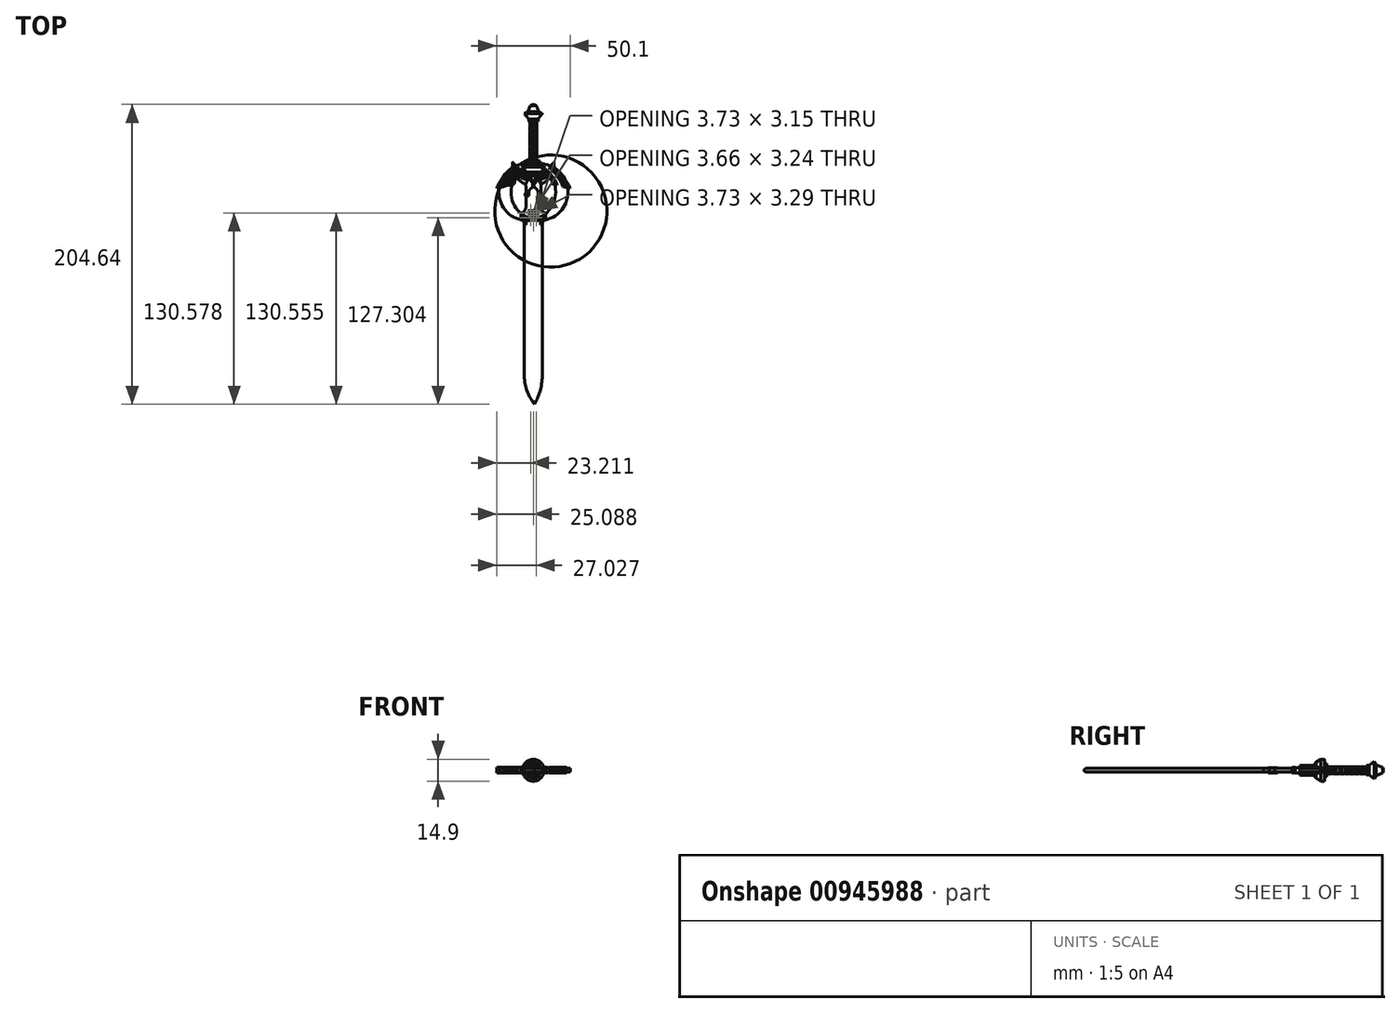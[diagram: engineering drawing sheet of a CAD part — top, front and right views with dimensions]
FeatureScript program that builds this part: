
annotation { "Feature Type Name" : "Feature", "Feature Type Description" : "" }
export const myFeature = defineFeature(function(context is Context, id is Id, definition is map)
    precondition{}
    {
        {
            var Q0;
            Q0=qCreatedBy(makeId("Top.planeOp"),FACE);
            var sketch = newSketch(context, id + "F0", { "sketchPlane" : qUnion([Q0])});
            skLineSegment(sketch, "E0", {"start": v(-5.22, 76.34) * mm, "end": v(-7.23, 75.61) * mm});
            skLineSegment(sketch, "E1", {"start": v(-7.23, 75.61) * mm, "end": v(-8.9, 71.32) * mm});
            skLineSegment(sketch, "E2", {"start": v(-8.9, 71.32) * mm, "end": v(-11.32, 70.05) * mm});
            skLineSegment(sketch, "E3", {"start": v(-11.32, 70.05) * mm, "end": v(-8.36, 66.38) * mm});
            skLineSegment(sketch, "E4", {"start": v(-8.36, 66.38) * mm, "end": v(-8.36, 64.56) * mm});
            skLineSegment(sketch, "E5", {"start": v(-8.36, 64.56) * mm, "end": v(-7.6, 64.56) * mm});
            skLineSegment(sketch, "E6", {"start": v(-7.6, 64.56) * mm, "end": v(-7.6, 37.58) * mm});
            skLineSegment(sketch, "E7", {"start": v(-7.6, 37.58) * mm, "end": v(-9.75, 37.58) * mm});
            skLineSegment(sketch, "E8", {"start": v(-9.75, 37.58) * mm, "end": v(-9.75, 35.78) * mm});
            skLineSegment(sketch, "E9", {"start": v(-9.75, 35.78) * mm, "end": v(-12.69, 35.78) * mm});
            skLineSegment(sketch, "E10", {"start": v(-12.69, 35.78) * mm, "end": v(-12.69, 33.54) * mm});
            skLineSegment(sketch, "E11", {"start": v(-12.69, 33.54) * mm, "end": v(-10.65, 30.07) * mm});
            skLineSegment(sketch, "E12", {"start": v(-10.65, 30.07) * mm, "end": v(-9.23, 28.83) * mm});
            skLineSegment(sketch, "E13", {"start": v(-9.23, 28.83) * mm, "end": v(-6.85, 28.22) * mm});
            skLineSegment(sketch, "E14", {"start": v(-6.85, 28.22) * mm, "end": v(-5.24, 30.4) * mm});
            skLineSegment(sketch, "E15", {"start": v(-5.24, 30.4) * mm, "end": v(-5.22, 76.34) * mm});
            skLineSegment(sketch, "E16", {"start": v(-10.65, 30.07) * mm, "end": v(-10.65, 29.62) * mm});
            skPoint(sketch, "E17.1.internal.snap0", {"position": v(-11.67, 31.8) * mm});
            skFitSpline(sketch, "E17", {"points": [v(-10.65, 29.62) * mm, v(-11.67, 30.16) * mm, v(-14.84, 32.47) * mm, v(-17.18, 34.56) * mm, v(-19.44, 37) * mm], "startDerivative": vector(-5.37, 2.5) * mm, "endDerivative": vector(-8.35, 9.25) * mm});
            skFitSpline(sketch, "E18", {"points": [v(-19.44, 37) * mm, v(-19.44, 35.95) * mm, v(-19.44, 33.83) * mm, v(-19.4, 33.07) * mm, v(-19.44, 33.1) * mm], "startDerivative": vector(0.06, -3.26) * mm, "endDerivative": vector(-1.19, 0.34) * mm});
            skArc(sketch, "E19", {"start": v(-19.4, 33.07) * mm, "mid": v(-25.78, 26.83) * mm, "end": v(-30.3, 19.12) * mm});
            skLineSegment(sketch, "E20", {"start": v(-30.3, 19.12) * mm, "end": v(-18.17, 22.24) * mm});
            skArc(sketch, "E21", {"start": v(-16.35, 26.26) * mm, "mid": v(-17.68, 24.44) * mm, "end": v(-18.17, 22.24) * mm});
            skArc(sketch, "E22", {"start": v(-16.35, 26.26) * mm, "mid": v(-13.8, 23.71) * mm, "end": v(-10.63, 21.98) * mm});
            skArc(sketch, "E23", {"start": v(-16.56, 33.95) * mm, "mid": v(-23.15, 27.52) * mm, "end": v(-28.02, 19.7) * mm});
            skArc(sketch, "E24", {"start": v(-15.75, 33.22) * mm, "mid": v(-21.45, 27.4) * mm, "end": v(-25.51, 20.35) * mm});
            skArc(sketch, "E25", {"start": v(-14.84, 32.47) * mm, "mid": v(-20.11, 27.25) * mm, "end": v(-23.78, 20.8) * mm});
            skArc(sketch, "E26", {"start": v(-14.1, 31.89) * mm, "mid": v(-18.47, 27.05) * mm, "end": v(-21.62, 21.35) * mm});
            skArc(sketch, "E27", {"start": v(-13.5, 31.43) * mm, "mid": v(-17.34, 27.1) * mm, "end": v(-19.75, 21.83) * mm});
            skLineSegment(sketch, "E28", {"start": v(-16.35, 26.26) * mm, "end": v(-12.92, 31) * mm});
            skLineSegment(sketch, "E29", {"start": v(-19.4, 33.07) * mm, "end": v(-17.18, 34.56) * mm});
            skArc(sketch, "E30", {"start": v(-15.35, 27.65) * mm, "mid": v(-12.5, 25.83) * mm, "end": v(-9.23, 24.95) * mm});
            skArc(sketch, "E31", {"start": v(-14.49, 28.83) * mm, "mid": v(-11.25, 27.44) * mm, "end": v(-7.76, 26.93) * mm});
            skArc(sketch, "E32", {"start": v(-13.57, 30.1) * mm, "mid": v(-10.47, 28.76) * mm, "end": v(-7.17, 28) * mm});
            skLineSegment(sketch, "E33", {"start": v(-6.85, 28.22) * mm, "end": v(-10.63, 21.98) * mm});
            skFitSpline(sketch, "E34", {"points": [v(-9.23, 24.95) * mm, v(-8.83, 24.95) * mm], "startDerivative": vector(0.4, 0) * mm, "endDerivative": vector(0.4, 0) * mm});
            skFitSpline(sketch, "E35", {"points": [v(-7.76, 26.93) * mm, v(-7.63, 26.93) * mm], "startDerivative": vector(0.13, 0) * mm, "endDerivative": vector(0.13, 0) * mm});
            skFitSpline(sketch, "E36", {"points": [v(-7.17, 28) * mm, v(-7, 27.99) * mm], "startDerivative": vector(0.17, -0.02) * mm, "endDerivative": vector(0.17, -0.02) * mm});
            skFitSpline(sketch, "E37.MirrorCS", {"points": [v(8.96, 36.98) * mm, v(8.96, 35.93) * mm, v(8.96, 33.81) * mm, v(8.9, 33.06) * mm, v(8.96, 33.08) * mm], "startDerivative": vector(-0.07, -3.26) * mm, "endDerivative": vector(1.19, 0.34) * mm});
            skLineSegment(sketch, "E38.MirrorCS", {"start": v(8.9, 33.06) * mm, "end": v(6.7, 34.54) * mm});
            skLineSegment(sketch, "E39.MirrorCS", {"start": v(5.86, 26.25) * mm, "end": v(2.43, 31) * mm});
            skLineSegment(sketch, "E40.MirrorCS", {"start": v(2.2, 35.77) * mm, "end": v(2.2, 33.53) * mm});
            skPoint(sketch, "E41.MirrorP", {"position": v(1.18, 31.8) * mm});
            skArc(sketch, "E42.MirrorCS", {"start": v(3.62, 31.88) * mm, "mid": v(7.97, 27.04) * mm, "end": v(11.12, 21.33) * mm});
            skArc(sketch, "E43.MirrorCS", {"start": v(5.27, 33.2) * mm, "mid": v(10.96, 27.4) * mm, "end": v(15.01, 20.33) * mm});
            skArc(sketch, "E44.MirrorCS", {"start": v(5.86, 26.25) * mm, "mid": v(7.18, 24.42) * mm, "end": v(7.67, 22.22) * mm});
            skArc(sketch, "E45.MirrorCS", {"start": v(4.36, 32.46) * mm, "mid": v(9.62, 27.23) * mm, "end": v(13.28, 20.78) * mm});
            skArc(sketch, "E46.MirrorCS", {"start": v(3, 31.42) * mm, "mid": v(6.85, 27.09) * mm, "end": v(9.25, 21.82) * mm});
            skLineSegment(sketch, "E47.MirrorCS", {"start": v(0.16, 30.07) * mm, "end": v(0.16, 29.61) * mm});
            skFitSpline(sketch, "E48.MirrorCS", {"points": [v(0.16, 29.61) * mm, v(1.18, 30.15) * mm, v(4.36, 32.46) * mm, v(6.7, 34.54) * mm, v(8.96, 36.98) * mm], "startDerivative": vector(5.37, 2.5) * mm, "endDerivative": vector(8.36, 9.24) * mm});
            skLineSegment(sketch, "E49.MirrorCS", {"start": v(2.2, 33.53) * mm, "end": v(0.16, 30.07) * mm});
            skArc(sketch, "E50.MirrorCS", {"start": v(5.86, 26.25) * mm, "mid": v(3.3, 23.7) * mm, "end": v(0.14, 21.97) * mm});
            skArc(sketch, "E51.MirrorCS", {"start": v(6.07, 33.93) * mm, "mid": v(12.66, 27.5) * mm, "end": v(17.52, 19.68) * mm});
            skArc(sketch, "E52.MirrorCS", {"start": v(8.9, 33.06) * mm, "mid": v(15.29, 26.8) * mm, "end": v(19.8, 19.1) * mm});
            skLineSegment(sketch, "E53.MirrorCS", {"start": v(19.8, 19.1) * mm, "end": v(7.67, 22.22) * mm});
            skFitSpline(sketch, "E54.MirrorCS", {"points": [v(0.16, 29.61) * mm, v(1.18, 30.15) * mm, v(4.36, 32.46) * mm, v(6.7, 34.54) * mm, v(8.96, 36.98) * mm], "startDerivative": vector(5.37, 2.5) * mm, "endDerivative": vector(8.36, 9.24) * mm});
            skArc(sketch, "E55.MirrorCS", {"start": v(4.86, 27.64) * mm, "mid": v(2, 25.82) * mm, "end": v(-1.27, 24.95) * mm});
            skArc(sketch, "E56.MirrorCS", {"start": v(4, 28.82) * mm, "mid": v(0.76, 27.43) * mm, "end": v(-2.73, 26.93) * mm});
            skArc(sketch, "E57.MirrorCS", {"start": v(3.08, 30.1) * mm, "mid": v(-0.02, 28.75) * mm, "end": v(-3.32, 28) * mm});
            skLineSegment(sketch, "E58.MirrorCS", {"start": v(-3.64, 28.22) * mm, "end": v(0.14, 21.97) * mm});
            skLineSegment(sketch, "E59.MirrorCS", {"start": v(0.16, 30.07) * mm, "end": v(-1.26, 28.83) * mm});
            skLineSegment(sketch, "E60.MirrorCS", {"start": v(-1.26, 28.83) * mm, "end": v(-3.64, 28.22) * mm});
            skFitSpline(sketch, "E61.MirrorCS", {"points": [v(-3.32, 28) * mm, v(-3.5, 27.99) * mm], "startDerivative": vector(-0.17, -0.02) * mm, "endDerivative": vector(-0.17, -0.02) * mm});
            skFitSpline(sketch, "E62.MirrorCS", {"points": [v(-2.73, 26.93) * mm, v(-2.86, 26.93) * mm], "startDerivative": vector(-0.13, 0) * mm, "endDerivative": vector(-0.13, 0) * mm});
            skFitSpline(sketch, "E63.MirrorCS", {"points": [v(-1.27, 24.95) * mm, v(-1.66, 24.95) * mm], "startDerivative": vector(-0.4, 0) * mm, "endDerivative": vector(-0.4, 0) * mm});
            skFitSpline(sketch, "E64", {"points": [v(-10.63, 21.98) * mm, v(-10.33, 20.1) * mm, v(-10.37, 18.46) * mm, v(-10.37, 16.67) * mm, v(-10.36, 15.95) * mm], "startDerivative": vector(1.43, -6.77) * mm, "endDerivative": vector(0.02, -3.56) * mm});
            skLineSegment(sketch, "E65", {"start": v(-10.36, 15.95) * mm, "end": v(-8.26, 15.95) * mm});
            skFitSpline(sketch, "E66", {"points": [v(-8.26, 15.95) * mm, v(-8.26, 16.44) * mm, v(-8.13, 17.45) * mm, v(-7.66, 18.2) * mm, v(-6.66, 19.28) * mm, v(-6, 19.75) * mm, v(-5.8, 19.83) * mm], "startDerivative": vector(-0.06, 3.2) * mm, "endDerivative": vector(1.98, 0.65) * mm});
            skFitSpline(sketch, "E67", {"points": [v(-4.62, 19.83) * mm, v(-3.94, 19.37) * mm, v(-3.02, 18.52) * mm, v(-2.42, 17.82) * mm, v(-2.16, 17.16) * mm, v(-2.1, 16.47) * mm, v(-2.1, 15.95) * mm], "startDerivative": vector(3.91, -2.38) * mm, "endDerivative": vector(0.1, -3.68) * mm});
            skLineSegment(sketch, "E68", {"start": v(-2.1, 15.95) * mm, "end": v(-0.16, 15.95) * mm});
            skFitSpline(sketch, "E69.MirrorCS", {"points": [v(0.14, 21.97) * mm, v(-0.17, 20.1) * mm, v(-0.13, 18.46) * mm, v(-0.13, 16.66) * mm, v(-0.14, 15.95) * mm], "startDerivative": vector(-1.44, -6.76) * mm, "endDerivative": vector(-0.02, -3.56) * mm});
            skLineSegment(sketch, "E70", {"start": v(-0.16, 15.95) * mm, "end": v(-0.14, 15.95) * mm});
            skLineSegment(sketch, "E71", {"start": v(-3.64, 28.22) * mm, "end": v(-5.24, 30.4) * mm});
            skLineSegment(sketch, "E72", {"start": v(-8.15, 26.08) * mm, "end": v(-5.86, 22.58) * mm});
            skLineSegment(sketch, "E73", {"start": v(-5.86, 22.58) * mm, "end": v(-5.8, 19.83) * mm});
            skLineSegment(sketch, "E74.MirrorCS", {"start": v(-2.34, 26.08) * mm, "end": v(-4.63, 22.58) * mm});
            skLineSegment(sketch, "E75.MirrorCS", {"start": v(-4.63, 22.58) * mm, "end": v(-4.7, 19.83) * mm});
            skLineSegment(sketch, "E76", {"start": v(-4.7, 19.83) * mm, "end": v(-4.62, 19.83) * mm});
            skLineSegment(sketch, "E77", {"start": v(-10.36, 15.95) * mm, "end": v(-10.95, 15.95) * mm});
            skLineSegment(sketch, "E78", {"start": v(-10.95, 15.95) * mm, "end": v(-10.95, 13.83) * mm});
            skLineSegment(sketch, "E79", {"start": v(-10.95, 13.83) * mm, "end": v(-8.63, 13.83) * mm});
            skLineSegment(sketch, "E80", {"start": v(-8.63, 13.83) * mm, "end": v(-8.27, 13.83) * mm});
            skLineSegment(sketch, "E81", {"start": v(-8.27, 13.83) * mm, "end": v(-8.26, 15.95) * mm});
            skLineSegment(sketch, "E82", {"start": v(-2.1, 15.95) * mm, "end": v(-2.1, 13.83) * mm});
            skLineSegment(sketch, "E83", {"start": v(-2.1, 13.83) * mm, "end": v(0.52, 13.83) * mm});
            skLineSegment(sketch, "E84", {"start": v(0.52, 13.83) * mm, "end": v(0.52, 15.95) * mm});
            skLineSegment(sketch, "E85", {"start": v(0.52, 15.95) * mm, "end": v(-0.16, 15.95) * mm});
            skLineSegment(sketch, "E86", {"start": v(-10.95, 15.26) * mm, "end": v(-8.26, 15.26) * mm});
            skLineSegment(sketch, "E87", {"start": v(-10.95, 14.53) * mm, "end": v(-8.26, 14.53) * mm});
            skLineSegment(sketch, "E88", {"start": v(-2.1, 15.22) * mm, "end": v(0.52, 15.22) * mm});
            skLineSegment(sketch, "E89", {"start": v(-2.1, 14.56) * mm, "end": v(0.52, 14.56) * mm});
            skLineSegment(sketch, "E90", {"start": v(-10.16, 13.83) * mm, "end": v(-10.16, 7.22) * mm});
            skArc(sketch, "E91", {"start": v(-13.54, 1.97) * mm, "mid": v(-11.08, 4.1) * mm, "end": v(-10.16, 7.22) * mm});
            skLineSegment(sketch, "E92", {"start": v(-13.54, 1.97) * mm, "end": v(-13.54, -1.9) * mm});
            skFitSpline(sketch, "E93", {"points": [v(-13.54, -1.9) * mm, v(-12.3, -3.14) * mm, v(-11.8, -3.88) * mm, v(-11.55, -4.81) * mm, v(-11.55, -5.66) * mm], "startDerivative": vector(4.34, -4.17) * mm, "endDerivative": vector(-0.22, -3.77) * mm});
            skLineSegment(sketch, "E94", {"start": v(-11.55, -5.66) * mm, "end": v(-11.55, -107.82) * mm});
            skLineSegment(sketch, "E95.MirrorCS", {"start": v(1.02, -5.67) * mm, "end": v(0.91, -107.82) * mm});
            skLineSegment(sketch, "E96.MirrorCS", {"start": v(-0.34, 13.83) * mm, "end": v(-0.35, 7.21) * mm});
            skArc(sketch, "E97.MirrorCS", {"start": v(3.03, 1.96) * mm, "mid": v(0.56, 4.1) * mm, "end": v(-0.35, 7.21) * mm});
            skLineSegment(sketch, "E98.MirrorCS", {"start": v(3.03, 1.96) * mm, "end": v(3.02, -1.91) * mm});
            skFitSpline(sketch, "E99.MirrorCS", {"points": [v(3.02, -1.91) * mm, v(1.78, -3.15) * mm, v(1.28, -3.9) * mm, v(1.02, -4.82) * mm, v(1.02, -5.67) * mm], "startDerivative": vector(-4.35, -4.17) * mm, "endDerivative": vector(0.22, -3.77) * mm});
            skArc(sketch, "E100", {"start": v(-11.55, -107.82) * mm, "mid": v(-9.73, -118.65) * mm, "end": v(-4.5, -128.3) * mm});
            skArc(sketch, "E101", {"start": v(-4.5, -128.3) * mm, "mid": v(-0.47, -118.4) * mm, "end": v(0.91, -107.82) * mm});
            skLineSegment(sketch, "E102", {"start": v(-4.7, 19.83) * mm, "end": v(-5.24, 19.13) * mm});
            skLineSegment(sketch, "E103", {"start": v(-5.24, 19.13) * mm, "end": v(-5.8, 19.83) * mm});
            skLineSegment(sketch, "E104", {"start": v(-0.34, 13.83) * mm, "end": v(-0.34, 13.83) * mm});
            skSolve(sketch);
        }
        {
            var Q0;
            Q0=makeQuery(id+"F0.imprint","IMPRINT",FACE,{"disambiguationData":[TD([[makeQuery(id+"F0.imprint","IMPRINT",EDGE,{"derivedFrom":sQuery(id+"F0.wireOp",EDGE,"E0")}),1.0]])]});
            var Q1;
            Q1=sQuery(id+"F0.wireOp",EDGE,"E15");
            revolve(context, id + "F1", {"surfaceOperationType" : NewSurfaceOperationType.NEW, "entities" : qUnion([Q0]), "axis" : qUnion([Q1]), "revolveType" : RevolveType.FULL});
        }
        {
            var Q0;
            {var subQ1=sQuery(id+"F0.wireOp",EDGE,"E22");Q0=makeQuery(id+"F0.imprint","IMPRINT",FACE,{"disambiguationData":[TD([[makeQuery(id+"F0.imprint","IMPRINT",EDGE,{"derivedFrom":subQ1}),1.0]])]});}
            var Q1;
            {var subQ2=sQuery(id+"F0.wireOp",EDGE,"E19");Q1=makeQuery(id+"F0.imprint","IMPRINT",FACE,{"disambiguationData":[TD([[makeQuery(id+"F0.imprint","IMPRINT",EDGE,{"derivedFrom":subQ2}),1.0]])]});}
            var Q2;
            {var subQ3=sQuery(id+"F0.wireOp",EDGE,"E55.MirrorCS");Q2=makeQuery(id+"F0.imprint","IMPRINT",FACE,{"disambiguationData":[TD([[makeQuery(id+"F0.imprint","IMPRINT",EDGE,{"derivedFrom":subQ3}),1.0]])]});}
            var Q3;
            {var subQ5=sQuery(id+"F0.wireOp",EDGE,"E51.MirrorCS");Q3=makeQuery(id+"F0.imprint","IMPRINT",FACE,{"disambiguationData":[TD([[makeQuery(id+"F0.imprint","IMPRINT",EDGE,{"derivedFrom":subQ5}),1.0]])]});}
            extrude(context, id + "F2", {"entities" : qUnion([Q0, Q1, Q2, Q3]), "endBound" : BoundingType.SYMMETRIC, "depth" : 3.86 * mm, "offsetDistance" : 25.4 * mm});
        }
        {
            var Q0;
            {var subQ0=sQuery(id+"F0.wireOp",EDGE,"E23");Q0=makeQuery(id+"F0.imprint","IMPRINT",FACE,{"disambiguationData":[TD([[makeQuery(id+"F0.imprint","IMPRINT",EDGE,{"derivedFrom":subQ0}),1.0]])]});}
            var Q1;
            {var subQ4=sQuery(id+"F0.wireOp",EDGE,"E30");Q1=makeQuery(id+"F0.imprint","IMPRINT",FACE,{"disambiguationData":[TD([[makeQuery(id+"F0.imprint","IMPRINT",EDGE,{"derivedFrom":subQ4}),1.0]])]});}
            var Q2;
            {var subQ3=sQuery(id+"F0.wireOp",EDGE,"E55.MirrorCS");Q2=makeQuery(id+"F0.imprint","IMPRINT",FACE,{"disambiguationData":[TD([[makeQuery(id+"F0.imprint","IMPRINT",EDGE,{"derivedFrom":subQ3}),-1.0]])]});}
            var Q3;
            {var subQ0=sQuery(id+"F0.wireOp",EDGE,"E51.MirrorCS");Q3=makeQuery(id+"F0.imprint","IMPRINT",FACE,{"disambiguationData":[TD([[makeQuery(id+"F0.imprint","IMPRINT",EDGE,{"derivedFrom":subQ0}),-1.0]])]});}
            extrude(context, id + "F3", {"entities" : qUnion([Q0, Q1, Q2, Q3]), "endBound" : BoundingType.SYMMETRIC, "depth" : 2.54 * mm, "offsetDistance" : 25.4 * mm});
        }
        {
            var Q0;
            {var subQ0=sQuery(id+"F0.wireOp",EDGE,"E24");Q0=makeQuery(id+"F0.imprint","IMPRINT",FACE,{"disambiguationData":[TD([[makeQuery(id+"F0.imprint","IMPRINT",EDGE,{"derivedFrom":subQ0}),1.0]])]});}
            var Q1;
            {var subQ4=sQuery(id+"F0.wireOp",EDGE,"E31");Q1=makeQuery(id+"F0.imprint","IMPRINT",FACE,{"disambiguationData":[TD([[makeQuery(id+"F0.imprint","IMPRINT",EDGE,{"derivedFrom":subQ4}),1.0]])]});}
            var Q2;
            {var subQ0=sQuery(id+"F0.wireOp",EDGE,"E43.MirrorCS");Q2=makeQuery(id+"F0.imprint","IMPRINT",FACE,{"disambiguationData":[TD([[makeQuery(id+"F0.imprint","IMPRINT",EDGE,{"derivedFrom":subQ0}),-1.0]])]});}
            var Q3;
            {var subQ3=sQuery(id+"F0.wireOp",EDGE,"E56.MirrorCS");Q3=makeQuery(id+"F0.imprint","IMPRINT",FACE,{"disambiguationData":[TD([[makeQuery(id+"F0.imprint","IMPRINT",EDGE,{"derivedFrom":subQ3}),-1.0]])]});}
            extrude(context, id + "F4", {"entities" : qUnion([Q0, Q1, Q2, Q3]), "endBound" : BoundingType.SYMMETRIC, "depth" : 1.93 * mm, "offsetDistance" : 25.4 * mm});
        }
        {
            var Q0;
            Q0=makeQuery(id+"F0.imprint","IMPRINT",FACE,{"disambiguationData":[TD([[makeQuery(id+"F0.imprint","IMPRINT",EDGE,{"derivedFrom":sQuery(id+"F0.wireOp",EDGE,"E12")}),-1.0]])]});
            var Q1;
            {var subQ0=sQuery(id+"F0.wireOp",EDGE,"E25");Q1=makeQuery(id+"F0.imprint","IMPRINT",FACE,{"disambiguationData":[TD([[makeQuery(id+"F0.imprint","IMPRINT",EDGE,{"derivedFrom":subQ0}),1.0]])]});}
            var Q2;
            {var subQ2=sQuery(id+"F0.wireOp",EDGE,"E47.MirrorCS");Q2=makeQuery(id+"F0.imprint","IMPRINT",FACE,{"disambiguationData":[TD([[makeQuery(id+"F0.imprint","IMPRINT",EDGE,{"derivedFrom":subQ2}),-1.0]])]});}
            var Q3;
            {var subQ0=sQuery(id+"F0.wireOp",EDGE,"E42.MirrorCS");Q3=makeQuery(id+"F0.imprint","IMPRINT",FACE,{"disambiguationData":[TD([[makeQuery(id+"F0.imprint","IMPRINT",EDGE,{"derivedFrom":subQ0}),1.0]])]});}
            extrude(context, id + "F5", {"entities" : qUnion([Q0, Q1, Q2, Q3]), "endBound" : BoundingType.SYMMETRIC, "depth" : 1.47 * mm, "offsetDistance" : 25.4 * mm});
        }
        {
            var Q0;
            {var subQ0=sQuery(id+"F0.wireOp",EDGE,"E46.MirrorCS");Q0=makeQuery(id+"F0.imprint","IMPRINT",FACE,{"disambiguationData":[TD([[makeQuery(id+"F0.imprint","IMPRINT",EDGE,{"derivedFrom":subQ0}),1.0]])]});}
            var Q1;
            {var subQ0=sQuery(id+"F0.wireOp",EDGE,"E26");Q1=makeQuery(id+"F0.imprint","IMPRINT",FACE,{"disambiguationData":[TD([[makeQuery(id+"F0.imprint","IMPRINT",EDGE,{"derivedFrom":subQ0}),1.0]])]});}
            extrude(context, id + "F6", {"entities" : qUnion([Q0, Q1]), "endBound" : BoundingType.SYMMETRIC, "oppositeDirection" : true, "depth" : 1.02 * mm, "offsetDistance" : 25.4 * mm});
        }
        {
            var Q0;
            {var subQ6=sQuery(id+"F0.wireOp",EDGE,"E44.MirrorCS");Q0=makeQuery(id+"F0.imprint","IMPRINT",FACE,{"disambiguationData":[TD([[makeQuery(id+"F0.imprint","IMPRINT",EDGE,{"derivedFrom":subQ6}),1.0]])]});}
            var Q1;
            {var subQ1=sQuery(id+"F0.wireOp",EDGE,"E21");Q1=makeQuery(id+"F0.imprint","IMPRINT",FACE,{"disambiguationData":[TD([[makeQuery(id+"F0.imprint","IMPRINT",EDGE,{"derivedFrom":subQ1}),-1.0]])]});}
            extrude(context, id + "F7", {"entities" : qUnion([Q0, Q1]), "endBound" : BoundingType.SYMMETRIC, "depth" : 0.76 * mm, "offsetDistance" : 25.4 * mm});
        }
        {
            var Q0;
            {var subQ6=sQuery(id+"F0.wireOp",EDGE,"E14");Q0=makeQuery(id+"F0.imprint","IMPRINT",FACE,{"disambiguationData":[TD([[makeQuery(id+"F0.imprint","IMPRINT",EDGE,{"derivedFrom":subQ6}),-1.0]])]});}
            extrude(context, id + "F8", {"entities" : qUnion([Q0]), "endBound" : BoundingType.SYMMETRIC, "depth" : 6.6 * mm, "offsetDistance" : 25.4 * mm});
        }
        {
            var Q0;
            Q0=makeQuery(id+"F0.imprint","IMPRINT",FACE,{"disambiguationData":[TD([[makeQuery(id+"F0.imprint","IMPRINT",EDGE,{"derivedFrom":sQuery(id+"F0.wireOp",EDGE,"E67")}),1.0]])]});
            var Q1;
            {var subQ0=sQuery(id+"F0.wireOp",EDGE,"E64");Q1=makeQuery(id+"F0.imprint","IMPRINT",FACE,{"disambiguationData":[TD([[makeQuery(id+"F0.imprint","IMPRINT",EDGE,{"derivedFrom":subQ0}),1.0]])]});}
            extrude(context, id + "F9", {"entities" : qUnion([Q0, Q1]), "endBound" : BoundingType.SYMMETRIC, "depth" : 3.56 * mm, "offsetDistance" : 25.4 * mm});
        }
        {
            var Q0;
            Q0=makeQuery(id+"F8.opExtrude","CAP_EDGE",EDGE,{"disambiguationData":[OSD([sQuery(id+"F0.wireOp",EDGE,"E33")])],"isStart":false});
            var Q1;
            Q1=makeQuery(id+"F8.opExtrude","CAP_EDGE",EDGE,{"disambiguationData":[OSD([sQuery(id+"F0.wireOp",EDGE,"E58.MirrorCS")])],"isStart":false});
            var Q2;
            Q2=makeQuery(id+"F8.opExtrude","CAP_EDGE",EDGE,{"disambiguationData":[OSD([sQuery(id+"F0.wireOp",EDGE,"E72")])],"isStart":false});
            var Q3;
            Q3=makeQuery(id+"F8.opExtrude","CAP_EDGE",EDGE,{"disambiguationData":[OSD([sQuery(id+"F0.wireOp",EDGE,"E74.MirrorCS")])],"isStart":false});
            var Q4;
            Q4=makeQuery(id+"F8.opExtrude","CAP_EDGE",EDGE,{"disambiguationData":[OSD([sQuery(id+"F0.wireOp",EDGE,"E72")])],"isStart":true});
            var Q5;
            Q5=makeQuery(id+"F8.opExtrude","CAP_EDGE",EDGE,{"disambiguationData":[OSD([sQuery(id+"F0.wireOp",EDGE,"E33")])],"isStart":true});
            var Q6;
            Q6=makeQuery(id+"F8.opExtrude","CAP_EDGE",EDGE,{"disambiguationData":[OSD([sQuery(id+"F0.wireOp",EDGE,"E58.MirrorCS")])],"isStart":true});
            var Q7;
            Q7=makeQuery(id+"F8.opExtrude","CAP_EDGE",EDGE,{"disambiguationData":[OSD([sQuery(id+"F0.wireOp",EDGE,"E74.MirrorCS")])],"isStart":true});
            chamfer(context, id + "F10", {"entities" : qUnion([Q0, Q1, Q2, Q3, Q4, Q5, Q6, Q7]), "width" : 1.02 * mm, "tangentPropagation" : true});
        }
        {
            var Q0;
            Q0=makeQuery(id+"F8.opExtrude","CAP_EDGE",EDGE,{"disambiguationData":[OSD([sQuery(id+"F0.wireOp",EDGE,"E73")])],"isStart":false});
            var Q1;
            Q1=makeQuery(id+"F8.opExtrude","CAP_EDGE",EDGE,{"disambiguationData":[OSD([sQuery(id+"F0.wireOp",EDGE,"E75.MirrorCS")])],"isStart":false});
            var Q2;
            Q2=makeQuery(id+"F8.opExtrude","CAP_EDGE",EDGE,{"disambiguationData":[OSD([sQuery(id+"F0.wireOp",EDGE,"E73")])],"isStart":true});
            var Q3;
            Q3=makeQuery(id+"F8.opExtrude","CAP_EDGE",EDGE,{"disambiguationData":[OSD([sQuery(id+"F0.wireOp",EDGE,"E75.MirrorCS")])],"isStart":true});
            chamfer(context, id + "F11", {"entities" : qUnion([Q0, Q1, Q2, Q3]), "width" : 0.5 * mm, "tangentPropagation" : true});
        }
        {
            var Q0;
            {var subQ1=sQuery(id+"F0.wireOp",EDGE,"E65");Q0=makeQuery(id+"F0.imprint","IMPRINT",FACE,{"disambiguationData":[TD([[makeQuery(id+"F0.imprint","IMPRINT",EDGE,{"derivedFrom":subQ1}),-1.0]])]});}
            var Q1;
            {var subQ5=sQuery(id+"F0.wireOp",EDGE,"E68");Q1=makeQuery(id+"F0.imprint","IMPRINT",FACE,{"disambiguationData":[TD([[makeQuery(id+"F0.imprint","IMPRINT",EDGE,{"derivedFrom":subQ5}),-1.0]])]});}
            var Q2;
            {var subQ0=sQuery(id+"F0.wireOp",EDGE,"E80");Q2=makeQuery(id+"F0.imprint","IMPRINT",FACE,{"disambiguationData":[TD([[makeQuery(id+"F0.imprint","IMPRINT",EDGE,{"derivedFrom":subQ0}),1.0]])]});}
            var Q3;
            {var subQ0=sQuery(id+"F0.wireOp",EDGE,"E83");Q3=makeQuery(id+"F0.imprint","IMPRINT",FACE,{"disambiguationData":[TD([[makeQuery(id+"F0.imprint","IMPRINT",EDGE,{"derivedFrom":subQ0}),1.0]])]});}
            extrude(context, id + "F12", {"entities" : qUnion([Q0, Q1, Q2, Q3]), "endBound" : BoundingType.SYMMETRIC, "depth" : 3.91 * mm, "offsetDistance" : 25.4 * mm});
        }
        {
            var Q0;
            {var subQ0=sQuery(id+"F0.wireOp",EDGE,"E86");Q0=makeQuery(id+"F0.imprint","IMPRINT",FACE,{"disambiguationData":[TD([[makeQuery(id+"F0.imprint","IMPRINT",EDGE,{"derivedFrom":subQ0}),-1.0]])]});}
            var Q1;
            {var subQ0=sQuery(id+"F0.wireOp",EDGE,"E88");Q1=makeQuery(id+"F0.imprint","IMPRINT",FACE,{"disambiguationData":[TD([[makeQuery(id+"F0.imprint","IMPRINT",EDGE,{"derivedFrom":subQ0}),-1.0]])]});}
            extrude(context, id + "F13", {"entities" : qUnion([Q0, Q1]), "endBound" : BoundingType.SYMMETRIC, "depth" : 3.15 * mm, "offsetDistance" : 25.4 * mm});
        }
        {
            var Q0;
            {var subQ10=sQuery(id+"F0.wireOp",EDGE,"E66");Q0=makeQuery(id+"F0.imprint","IMPRINT",FACE,{"disambiguationData":[TD([[makeQuery(id+"F0.imprint","IMPRINT",EDGE,{"derivedFrom":subQ10}),-1.0]])]});}
            extrude(context, id + "F14", {"entities" : qUnion([Q0]), "endBound" : BoundingType.SYMMETRIC, "depth" : 2.54 * mm, "offsetDistance" : 25.4 * mm});
        }
        {
            var Q0;
            Q0=makeQuery(id+"F14.opExtrude","CAP_EDGE",EDGE,{"disambiguationData":[OSD([sQuery(id+"F0.wireOp",EDGE,"E96.MirrorCS")])],"isStart":false});
            var Q1;
            Q1=makeQuery(id+"F14.opExtrude","CAP_EDGE",EDGE,{"disambiguationData":[OSD([sQuery(id+"F0.wireOp",EDGE,"E90")])],"isStart":false});
            var Q2;
            Q2=makeQuery(id+"F14.opExtrude","CAP_EDGE",EDGE,{"disambiguationData":[OSD([sQuery(id+"F0.wireOp",EDGE,"E95.MirrorCS")])],"isStart":false});
            var Q3;
            Q3=makeQuery(id+"F14.opExtrude","CAP_EDGE",EDGE,{"disambiguationData":[OSD([sQuery(id+"F0.wireOp",EDGE,"E94")])],"isStart":false});
            fillet(context, id + "F15", {"entities" : qUnion([Q0, Q1, Q2, Q3]), "radius" : 1.27 * mm, "tangentPropagation" : true, "allowEdgeOverflow" : false});
        }
        {
            var Q0;
            Q0=makeQuery(id+"F14.opExtrude","CAP_EDGE",EDGE,{"disambiguationData":[OSD([sQuery(id+"F0.wireOp",EDGE,"E101")])],"isStart":true});
            var Q1;
            Q1=makeQuery(id+"F14.opExtrude","CAP_EDGE",EDGE,{"disambiguationData":[OSD([sQuery(id+"F0.wireOp",EDGE,"E100")])],"isStart":true});
            var Q2;
            Q2=makeQuery(id+"F14.opExtrude","CAP_EDGE",EDGE,{"disambiguationData":[OSD([sQuery(id+"F0.wireOp",EDGE,"E95.MirrorCS")])],"isStart":true});
            var Q3;
            Q3=makeQuery(id+"F14.opExtrude","CAP_EDGE",EDGE,{"disambiguationData":[OSD([sQuery(id+"F0.wireOp",EDGE,"E94")])],"isStart":true});
            var Q4;
            Q4=makeQuery(id+"F14.opExtrude","CAP_EDGE",EDGE,{"disambiguationData":[OSD([sQuery(id+"F0.wireOp",EDGE,"E91")])],"isStart":true});
            var Q5;
            Q5=makeQuery(id+"F14.opExtrude","CAP_EDGE",EDGE,{"disambiguationData":[OSD([sQuery(id+"F0.wireOp",EDGE,"E97.MirrorCS")])],"isStart":true});
            fillet(context, id + "F16", {"entities" : qUnion([Q0, Q1, Q2, Q3, Q4, Q5]), "radius" : 1.27 * mm, "tangentPropagation" : true, "allowEdgeOverflow" : false});
        }
        {
            var Q0;
            {var subQ0=sQuery(id+"F0.wireOp",EDGE,"E18");var subQ1=sQuery(id+"F0.wireOp",EDGE,"E17");var subQ2=makeQuery(id+"F0.imprint","INTERSECT",VERTEX,{"derivedFrom":[subQ1,subQ0]});Q0=makeQuery(id+"F0.imprint","IMPRINT",FACE,{"disambiguationData":[TD([[makeQuery(id+"F0.imprint","IMPRINT",EDGE,{"disambiguationData":[TD([[subQ2,1.0]])],"derivedFrom":subQ1}),1.0]])]});}
            var Q1;
            {var subQ0=sQuery(id+"F0.wireOp",EDGE,"E54.MirrorCS");var subQ1=sQuery(id+"F0.wireOp",EDGE,"E37.MirrorCS");var subQ2=makeQuery(id+"F0.imprint","INTERSECT",VERTEX,{"derivedFrom":[subQ1,subQ0]});Q1=makeQuery(id+"F0.imprint","IMPRINT",FACE,{"disambiguationData":[TD([[makeQuery(id+"F0.imprint","IMPRINT",EDGE,{"disambiguationData":[TD([[subQ2,-1.0]])],"derivedFrom":subQ1}),-1.0]])]});}
            extrude(context, id + "F17", {"entities" : qUnion([Q0, Q1]), "endBound" : BoundingType.SYMMETRIC, "depth" : 1.93 * mm, "offsetDistance" : 25.4 * mm});
        }
        {
            var Q0;
            Q0=qCreatedBy(makeId("Top.planeOp"),FACE);
            cPlane(context, id + "F18", {"entities" : qUnion([Q0]), "cplaneType" : CPlaneType.OFFSET, "offset" : 24.13 * mm, "width" : 152.4 * mm, "height" : 152.4 * mm});
        }
        {
            var Q0;
            Q0=qCreatedBy(id+"F18.planeOp",FACE);
            var sketch = newSketch(context, id + "F19", { "sketchPlane" : qUnion([Q0])});
            skArc(sketch, "E105", {"start": v(-7.6, 62.67) * mm, "mid": v(-6.27, 63.36) * mm, "end": v(-5.28, 64.5) * mm});
            skArc(sketch, "E106", {"start": v(-5.28, 64.5) * mm, "mid": v(-4.32, 63.35) * mm, "end": v(-2.9, 62.86) * mm});
            skArc(sketch, "E107", {"start": v(-7.64, 62.11) * mm, "mid": v(-6.32, 62.62) * mm, "end": v(-5.28, 63.57) * mm});
            skArc(sketch, "E108", {"start": v(-5.28, 63.57) * mm, "mid": v(-4.17, 62.68) * mm, "end": v(-2.83, 62.18) * mm});
            skArc(sketch, "E109", {"start": v(-5.28, 61.16) * mm, "mid": v(-6.44, 61.63) * mm, "end": v(-7.68, 61.7) * mm});
            skArc(sketch, "E110", {"start": v(-2.83, 61.57) * mm, "mid": v(-4.1, 61.58) * mm, "end": v(-5.28, 61.16) * mm});
            skArc(sketch, "E111", {"start": v(-5.25, 60.69) * mm, "mid": v(-6.41, 61.16) * mm, "end": v(-7.66, 61.22) * mm});
            skArc(sketch, "E112", {"start": v(-2.84, 61.09) * mm, "mid": v(-4.08, 61.09) * mm, "end": v(-5.25, 60.69) * mm});
            skArc(sketch, "E113", {"start": v(-7.66, 59.05) * mm, "mid": v(-6.33, 59.51) * mm, "end": v(-5.23, 60.4) * mm});
            skArc(sketch, "E114", {"start": v(-5.23, 60.4) * mm, "mid": v(-4.16, 59.48) * mm, "end": v(-2.83, 59.05) * mm});
            skArc(sketch, "E115", {"start": v(-7.66, 58.65) * mm, "mid": v(-6.37, 58.91) * mm, "end": v(-5.23, 59.56) * mm});
            skArc(sketch, "E116", {"start": v(-5.23, 59.56) * mm, "mid": v(-4.08, 58.91) * mm, "end": v(-2.8, 58.58) * mm});
            skArc(sketch, "E117", {"start": v(-5.23, 57.6) * mm, "mid": v(-6.38, 58.15) * mm, "end": v(-7.66, 58.24) * mm});
            skArc(sketch, "E118", {"start": v(-2.86, 58.1) * mm, "mid": v(-4.09, 58.04) * mm, "end": v(-5.23, 57.6) * mm});
            skArc(sketch, "E119", {"start": v(-5.23, 56.97) * mm, "mid": v(-6.37, 57.61) * mm, "end": v(-7.66, 57.86) * mm});
            skArc(sketch, "E120", {"start": v(-2.84, 57.54) * mm, "mid": v(-4.08, 57.45) * mm, "end": v(-5.23, 56.97) * mm});
            skLineSegment(sketch, "E121", {"start": v(-7.6, 62.67) * mm, "end": v(-7.64, 62.11) * mm});
            skLineSegment(sketch, "E122", {"start": v(-7.68, 61.7) * mm, "end": v(-7.66, 61.22) * mm});
            skLineSegment(sketch, "E123", {"start": v(-7.66, 59.05) * mm, "end": v(-7.66, 58.65) * mm});
            skLineSegment(sketch, "E124", {"start": v(-7.66, 58.24) * mm, "end": v(-7.66, 57.86) * mm});
            skLineSegment(sketch, "E125", {"start": v(-2.84, 57.54) * mm, "end": v(-2.86, 58.1) * mm});
            skLineSegment(sketch, "E126", {"start": v(-2.8, 58.58) * mm, "end": v(-2.83, 59.05) * mm});
            skLineSegment(sketch, "E127", {"start": v(-2.84, 61.09) * mm, "end": v(-2.83, 61.57) * mm});
            skLineSegment(sketch, "E128", {"start": v(-2.83, 62.18) * mm, "end": v(-2.9, 62.86) * mm});
            skArc(sketch, "E129", {"start": v(-7.68, 55.5) * mm, "mid": v(-6.34, 55.96) * mm, "end": v(-5.24, 56.84) * mm});
            skArc(sketch, "E130", {"start": v(-5.24, 56.84) * mm, "mid": v(-4.18, 55.93) * mm, "end": v(-2.85, 55.5) * mm});
            skArc(sketch, "E131", {"start": v(-7.68, 55.1) * mm, "mid": v(-6.39, 55.36) * mm, "end": v(-5.24, 56) * mm});
            skArc(sketch, "E132", {"start": v(-5.24, 56) * mm, "mid": v(-4.1, 55.36) * mm, "end": v(-2.82, 55.03) * mm});
            skArc(sketch, "E133", {"start": v(-5.24, 54.04) * mm, "mid": v(-6.4, 54.6) * mm, "end": v(-7.68, 54.68) * mm});
            skArc(sketch, "E134", {"start": v(-2.88, 54.54) * mm, "mid": v(-4.1, 54.5) * mm, "end": v(-5.24, 54.04) * mm});
            skArc(sketch, "E135", {"start": v(-5.24, 53.41) * mm, "mid": v(-6.39, 54.06) * mm, "end": v(-7.68, 54.3) * mm});
            skArc(sketch, "E136", {"start": v(-2.85, 53.99) * mm, "mid": v(-4.1, 53.9) * mm, "end": v(-5.24, 53.41) * mm});
            skLineSegment(sketch, "E137", {"start": v(-7.68, 55.5) * mm, "end": v(-7.68, 55.1) * mm});
            skLineSegment(sketch, "E138", {"start": v(-7.68, 54.68) * mm, "end": v(-7.68, 54.3) * mm});
            skLineSegment(sketch, "E139", {"start": v(-2.85, 53.99) * mm, "end": v(-2.88, 54.54) * mm});
            skLineSegment(sketch, "E140", {"start": v(-2.82, 55.03) * mm, "end": v(-2.85, 55.5) * mm});
            skArc(sketch, "E141", {"start": v(-7.55, 51.7) * mm, "mid": v(-6.22, 52.16) * mm, "end": v(-5.12, 53.04) * mm});
            skArc(sketch, "E142", {"start": v(-5.12, 53.04) * mm, "mid": v(-4.05, 52.13) * mm, "end": v(-2.72, 51.7) * mm});
            skArc(sketch, "E143", {"start": v(-7.55, 51.3) * mm, "mid": v(-6.26, 51.56) * mm, "end": v(-5.12, 52.2) * mm});
            skArc(sketch, "E144", {"start": v(-5.12, 52.2) * mm, "mid": v(-3.97, 51.56) * mm, "end": v(-2.7, 51.23) * mm});
            skArc(sketch, "E145", {"start": v(-5.12, 50.24) * mm, "mid": v(-6.27, 50.8) * mm, "end": v(-7.55, 50.89) * mm});
            skArc(sketch, "E146", {"start": v(-2.75, 50.74) * mm, "mid": v(-3.98, 50.7) * mm, "end": v(-5.12, 50.24) * mm});
            skArc(sketch, "E147", {"start": v(-5.12, 49.62) * mm, "mid": v(-6.26, 50.26) * mm, "end": v(-7.55, 50.5) * mm});
            skArc(sketch, "E148", {"start": v(-2.72, 50.19) * mm, "mid": v(-3.97, 50.1) * mm, "end": v(-5.12, 49.62) * mm});
            skLineSegment(sketch, "E149", {"start": v(-7.55, 51.7) * mm, "end": v(-7.55, 51.3) * mm});
            skLineSegment(sketch, "E150", {"start": v(-7.55, 50.89) * mm, "end": v(-7.55, 50.5) * mm});
            skLineSegment(sketch, "E151", {"start": v(-2.72, 50.19) * mm, "end": v(-2.75, 50.74) * mm});
            skLineSegment(sketch, "E152", {"start": v(-2.7, 51.23) * mm, "end": v(-2.72, 51.7) * mm});
            skArc(sketch, "E153", {"start": v(-7.7, 47.74) * mm, "mid": v(-6.37, 48.2) * mm, "end": v(-5.27, 49.1) * mm});
            skArc(sketch, "E154", {"start": v(-5.27, 49.1) * mm, "mid": v(-4.2, 48.18) * mm, "end": v(-2.87, 47.74) * mm});
            skArc(sketch, "E155", {"start": v(-7.7, 47.35) * mm, "mid": v(-6.41, 47.61) * mm, "end": v(-5.27, 48.25) * mm});
            skArc(sketch, "E156", {"start": v(-5.27, 48.25) * mm, "mid": v(-4.12, 47.61) * mm, "end": v(-2.85, 47.28) * mm});
            skArc(sketch, "E157", {"start": v(-5.27, 46.29) * mm, "mid": v(-6.42, 46.85) * mm, "end": v(-7.7, 46.94) * mm});
            skArc(sketch, "E158", {"start": v(-2.9, 46.8) * mm, "mid": v(-4.13, 46.74) * mm, "end": v(-5.27, 46.29) * mm});
            skArc(sketch, "E159", {"start": v(-5.27, 45.67) * mm, "mid": v(-6.41, 46.3) * mm, "end": v(-7.7, 46.55) * mm});
            skArc(sketch, "E160", {"start": v(-2.88, 46.24) * mm, "mid": v(-4.12, 46.15) * mm, "end": v(-5.27, 45.67) * mm});
            skLineSegment(sketch, "E161", {"start": v(-7.7, 47.74) * mm, "end": v(-7.7, 47.35) * mm});
            skLineSegment(sketch, "E162", {"start": v(-7.7, 46.94) * mm, "end": v(-7.7, 46.55) * mm});
            skLineSegment(sketch, "E163", {"start": v(-2.88, 46.24) * mm, "end": v(-2.9, 46.8) * mm});
            skLineSegment(sketch, "E164", {"start": v(-2.85, 47.28) * mm, "end": v(-2.87, 47.74) * mm});
            skArc(sketch, "E165", {"start": v(-7.65, 43.68) * mm, "mid": v(-6.32, 44.14) * mm, "end": v(-5.22, 45.03) * mm});
            skArc(sketch, "E166", {"start": v(-5.22, 45.03) * mm, "mid": v(-4.15, 44.12) * mm, "end": v(-2.82, 43.68) * mm});
            skArc(sketch, "E167", {"start": v(-7.65, 43.28) * mm, "mid": v(-6.36, 43.55) * mm, "end": v(-5.22, 44.2) * mm});
            skArc(sketch, "E168", {"start": v(-5.22, 44.2) * mm, "mid": v(-4.07, 43.55) * mm, "end": v(-2.8, 43.21) * mm});
            skArc(sketch, "E169", {"start": v(-5.22, 42.22) * mm, "mid": v(-6.37, 42.78) * mm, "end": v(-7.65, 42.87) * mm});
            skArc(sketch, "E170", {"start": v(-2.85, 42.73) * mm, "mid": v(-4.08, 42.68) * mm, "end": v(-5.22, 42.22) * mm});
            skArc(sketch, "E171", {"start": v(-5.22, 41.6) * mm, "mid": v(-6.36, 42.25) * mm, "end": v(-7.65, 42.49) * mm});
            skArc(sketch, "E172", {"start": v(-2.83, 42.17) * mm, "mid": v(-4.07, 42.09) * mm, "end": v(-5.22, 41.6) * mm});
            skLineSegment(sketch, "E173", {"start": v(-7.65, 43.68) * mm, "end": v(-7.65, 43.28) * mm});
            skLineSegment(sketch, "E174", {"start": v(-7.65, 42.87) * mm, "end": v(-7.65, 42.49) * mm});
            skLineSegment(sketch, "E175", {"start": v(-2.83, 42.17) * mm, "end": v(-2.85, 42.73) * mm});
            skLineSegment(sketch, "E176", {"start": v(-2.8, 43.21) * mm, "end": v(-2.82, 43.68) * mm});
            skArc(sketch, "E177", {"start": v(-7.67, 39.9) * mm, "mid": v(-6.34, 40.37) * mm, "end": v(-5.24, 41.25) * mm});
            skArc(sketch, "E178", {"start": v(-5.24, 41.25) * mm, "mid": v(-4.17, 40.34) * mm, "end": v(-2.84, 39.9) * mm});
            skArc(sketch, "E179", {"start": v(-7.67, 39.5) * mm, "mid": v(-6.38, 39.77) * mm, "end": v(-5.24, 40.41) * mm});
            skArc(sketch, "E180", {"start": v(-5.24, 40.41) * mm, "mid": v(-4.1, 39.77) * mm, "end": v(-2.82, 39.44) * mm});
            skArc(sketch, "E181", {"start": v(-5.24, 38.45) * mm, "mid": v(-6.4, 39) * mm, "end": v(-7.67, 39.1) * mm});
            skArc(sketch, "E182", {"start": v(-2.87, 38.95) * mm, "mid": v(-4.1, 38.9) * mm, "end": v(-5.24, 38.45) * mm});
            skArc(sketch, "E183", {"start": v(-5.24, 37.82) * mm, "mid": v(-6.38, 38.47) * mm, "end": v(-7.67, 38.71) * mm});
            skArc(sketch, "E184", {"start": v(-2.85, 38.4) * mm, "mid": v(-4.1, 38.31) * mm, "end": v(-5.24, 37.82) * mm});
            skLineSegment(sketch, "E185", {"start": v(-7.67, 39.9) * mm, "end": v(-7.67, 39.5) * mm});
            skLineSegment(sketch, "E186", {"start": v(-7.67, 39.1) * mm, "end": v(-7.67, 38.71) * mm});
            skLineSegment(sketch, "E187", {"start": v(-2.85, 38.4) * mm, "end": v(-2.87, 38.95) * mm});
            skLineSegment(sketch, "E188", {"start": v(-2.82, 39.44) * mm, "end": v(-2.84, 39.9) * mm});
            skSolve(sketch);
        }
        {
            var Q0;
            Q0=makeQuery(id+"F19.imprint","IMPRINT",FACE,{"disambiguationData":[TD([[makeQuery(id+"F19.imprint","IMPRINT",EDGE,{"derivedFrom":sQuery(id+"F19.wireOp",EDGE,"E105")}),-1.0]])]});
            var Q1;
            Q1=makeQuery(id+"F19.imprint","IMPRINT",FACE,{"disambiguationData":[TD([[makeQuery(id+"F19.imprint","IMPRINT",EDGE,{"derivedFrom":sQuery(id+"F19.wireOp",EDGE,"E109")}),1.0]])]});
            var Q2;
            Q2=makeQuery(id+"F19.imprint","IMPRINT",FACE,{"disambiguationData":[TD([[makeQuery(id+"F19.imprint","IMPRINT",EDGE,{"derivedFrom":sQuery(id+"F19.wireOp",EDGE,"E113")}),-1.0]])]});
            var Q3;
            Q3=makeQuery(id+"F19.imprint","IMPRINT",FACE,{"disambiguationData":[TD([[makeQuery(id+"F19.imprint","IMPRINT",EDGE,{"derivedFrom":sQuery(id+"F19.wireOp",EDGE,"E117")}),1.0]])]});
            extrude(context, id + "F20", {"entities" : qUnion([Q0, Q1, Q2, Q3]), "operationType" : NewBodyOperationType.REMOVE, "oppositeDirection" : true, "depth" : 27.46 * mm, "offsetDistance" : 25.4 * mm});
        }
        {
            var Q0;
            Q0=makeQuery(id+"F19.imprint","IMPRINT",FACE,{"disambiguationData":[TD([[makeQuery(id+"F19.imprint","IMPRINT",EDGE,{"derivedFrom":sQuery(id+"F19.wireOp",EDGE,"E129")}),-1.0]])]});
            var Q1;
            Q1=makeQuery(id+"F19.imprint","IMPRINT",FACE,{"disambiguationData":[TD([[makeQuery(id+"F19.imprint","IMPRINT",EDGE,{"derivedFrom":sQuery(id+"F19.wireOp",EDGE,"E133")}),1.0]])]});
            var Q2;
            Q2=makeQuery(id+"F19.imprint","IMPRINT",FACE,{"disambiguationData":[TD([[makeQuery(id+"F19.imprint","IMPRINT",EDGE,{"derivedFrom":sQuery(id+"F19.wireOp",EDGE,"E141")}),-1.0]])]});
            var Q3;
            Q3=makeQuery(id+"F19.imprint","IMPRINT",FACE,{"disambiguationData":[TD([[makeQuery(id+"F19.imprint","IMPRINT",EDGE,{"derivedFrom":sQuery(id+"F19.wireOp",EDGE,"E145")}),1.0]])]});
            var Q4;
            Q4=makeQuery(id+"F19.imprint","IMPRINT",FACE,{"disambiguationData":[TD([[makeQuery(id+"F19.imprint","IMPRINT",EDGE,{"derivedFrom":sQuery(id+"F19.wireOp",EDGE,"E153")}),-1.0]])]});
            var Q5;
            Q5=makeQuery(id+"F19.imprint","IMPRINT",FACE,{"disambiguationData":[TD([[makeQuery(id+"F19.imprint","IMPRINT",EDGE,{"derivedFrom":sQuery(id+"F19.wireOp",EDGE,"E157")}),1.0]])]});
            var Q6;
            Q6=makeQuery(id+"F19.imprint","IMPRINT",FACE,{"disambiguationData":[TD([[makeQuery(id+"F19.imprint","IMPRINT",EDGE,{"derivedFrom":sQuery(id+"F19.wireOp",EDGE,"E165")}),-1.0]])]});
            var Q7;
            Q7=makeQuery(id+"F19.imprint","IMPRINT",FACE,{"disambiguationData":[TD([[makeQuery(id+"F19.imprint","IMPRINT",EDGE,{"derivedFrom":sQuery(id+"F19.wireOp",EDGE,"E169")}),1.0]])]});
            var Q8;
            Q8=makeQuery(id+"F19.imprint","IMPRINT",FACE,{"disambiguationData":[TD([[makeQuery(id+"F19.imprint","IMPRINT",EDGE,{"derivedFrom":sQuery(id+"F19.wireOp",EDGE,"E177")}),-1.0]])]});
            var Q9;
            Q9=makeQuery(id+"F19.imprint","IMPRINT",FACE,{"disambiguationData":[TD([[makeQuery(id+"F19.imprint","IMPRINT",EDGE,{"derivedFrom":sQuery(id+"F19.wireOp",EDGE,"E181")}),1.0]])]});
            extrude(context, id + "F21", {"entities" : qUnion([Q0, Q1, Q2, Q3, Q4, Q5, Q6, Q7, Q8, Q9]), "operationType" : NewBodyOperationType.REMOVE, "oppositeDirection" : true, "depth" : 33.78 * mm, "offsetDistance" : 25.4 * mm});
        }
        {
            var Q0;
            Q0=qCreatedBy(makeId("Top.planeOp"),FACE);
            var sketch = newSketch(context, id + "F22", { "sketchPlane" : qUnion([Q0])});
            skLineSegment(sketch, "E189", {"start": v(-7.61, 54.25) * mm, "end": v(-7.61, 54.64) * mm});
            skArc(sketch, "E190", {"start": v(-7.67, 39.88) * mm, "mid": v(-6.34, 40.34) * mm, "end": v(-5.24, 41.23) * mm});
            skArc(sketch, "E191", {"start": v(-5.24, 41.23) * mm, "mid": v(-4.18, 40.32) * mm, "end": v(-2.85, 39.88) * mm});
            skArc(sketch, "E192", {"start": v(-7.67, 39.48) * mm, "mid": v(-6.39, 39.75) * mm, "end": v(-5.24, 40.39) * mm});
            skArc(sketch, "E193", {"start": v(-5.24, 40.39) * mm, "mid": v(-4.1, 39.75) * mm, "end": v(-2.82, 39.41) * mm});
            skArc(sketch, "E194", {"start": v(-5.24, 38.42) * mm, "mid": v(-6.4, 38.98) * mm, "end": v(-7.67, 39.07) * mm});
            skArc(sketch, "E195", {"start": v(-2.88, 38.93) * mm, "mid": v(-4.1, 38.88) * mm, "end": v(-5.24, 38.42) * mm});
            skArc(sketch, "E196", {"start": v(-5.24, 37.8) * mm, "mid": v(-6.39, 38.44) * mm, "end": v(-7.67, 38.69) * mm});
            skArc(sketch, "E197", {"start": v(-2.85, 38.37) * mm, "mid": v(-4.1, 38.29) * mm, "end": v(-5.24, 37.8) * mm});
            skLineSegment(sketch, "E198", {"start": v(-7.67, 39.88) * mm, "end": v(-7.67, 39.48) * mm});
            skLineSegment(sketch, "E199", {"start": v(-7.67, 39.07) * mm, "end": v(-7.67, 38.69) * mm});
            skLineSegment(sketch, "E200", {"start": v(-2.85, 38.37) * mm, "end": v(-2.88, 38.93) * mm});
            skLineSegment(sketch, "E201", {"start": v(-2.82, 39.41) * mm, "end": v(-2.85, 39.88) * mm});
            skArc(sketch, "E202", {"start": v(-7.58, 43.67) * mm, "mid": v(-6.25, 44.14) * mm, "end": v(-5.15, 45.02) * mm});
            skArc(sketch, "E203", {"start": v(-5.15, 45.02) * mm, "mid": v(-4.08, 44.11) * mm, "end": v(-2.75, 43.67) * mm});
            skArc(sketch, "E204", {"start": v(-7.58, 43.28) * mm, "mid": v(-6.3, 43.54) * mm, "end": v(-5.15, 44.19) * mm});
            skArc(sketch, "E205", {"start": v(-5.15, 44.19) * mm, "mid": v(-4, 43.54) * mm, "end": v(-2.73, 43.2) * mm});
            skArc(sketch, "E206", {"start": v(-5.15, 42.22) * mm, "mid": v(-6.3, 42.78) * mm, "end": v(-7.58, 42.87) * mm});
            skArc(sketch, "E207", {"start": v(-2.78, 42.72) * mm, "mid": v(-4, 42.67) * mm, "end": v(-5.15, 42.22) * mm});
            skArc(sketch, "E208", {"start": v(-5.15, 41.6) * mm, "mid": v(-6.29, 42.24) * mm, "end": v(-7.58, 42.48) * mm});
            skArc(sketch, "E209", {"start": v(-2.76, 42.17) * mm, "mid": v(-4, 42.08) * mm, "end": v(-5.15, 41.6) * mm});
            skLineSegment(sketch, "E210", {"start": v(-7.58, 43.67) * mm, "end": v(-7.58, 43.28) * mm});
            skLineSegment(sketch, "E211", {"start": v(-7.58, 42.87) * mm, "end": v(-7.58, 42.48) * mm});
            skLineSegment(sketch, "E212", {"start": v(-2.76, 42.17) * mm, "end": v(-2.78, 42.72) * mm});
            skLineSegment(sketch, "E213", {"start": v(-2.73, 43.2) * mm, "end": v(-2.75, 43.67) * mm});
            skArc(sketch, "E214", {"start": v(-7.7, 47.79) * mm, "mid": v(-6.38, 48.25) * mm, "end": v(-5.28, 49.14) * mm});
            skArc(sketch, "E215", {"start": v(-5.28, 49.14) * mm, "mid": v(-4.21, 48.22) * mm, "end": v(-2.88, 47.79) * mm});
            skArc(sketch, "E216", {"start": v(-7.7, 47.39) * mm, "mid": v(-6.42, 47.65) * mm, "end": v(-5.28, 48.3) * mm});
            skArc(sketch, "E217", {"start": v(-5.28, 48.3) * mm, "mid": v(-4.13, 47.65) * mm, "end": v(-2.86, 47.32) * mm});
            skArc(sketch, "E218", {"start": v(-5.28, 46.33) * mm, "mid": v(-6.43, 46.9) * mm, "end": v(-7.7, 46.98) * mm});
            skArc(sketch, "E219", {"start": v(-2.91, 46.84) * mm, "mid": v(-4.14, 46.78) * mm, "end": v(-5.28, 46.33) * mm});
            skArc(sketch, "E220", {"start": v(-5.28, 45.7) * mm, "mid": v(-6.42, 46.35) * mm, "end": v(-7.7, 46.6) * mm});
            skArc(sketch, "E221", {"start": v(-2.89, 46.28) * mm, "mid": v(-4.13, 46.2) * mm, "end": v(-5.28, 45.7) * mm});
            skLineSegment(sketch, "E222", {"start": v(-7.7, 47.79) * mm, "end": v(-7.7, 47.39) * mm});
            skLineSegment(sketch, "E223", {"start": v(-7.7, 46.98) * mm, "end": v(-7.7, 46.6) * mm});
            skLineSegment(sketch, "E224", {"start": v(-2.89, 46.28) * mm, "end": v(-2.91, 46.84) * mm});
            skLineSegment(sketch, "E225", {"start": v(-2.86, 47.32) * mm, "end": v(-2.88, 47.79) * mm});
            skArc(sketch, "E226", {"start": v(-7.5, 51.64) * mm, "mid": v(-6.18, 52.1) * mm, "end": v(-5.08, 53) * mm});
            skArc(sketch, "E227", {"start": v(-5.08, 53) * mm, "mid": v(-4.01, 52.08) * mm, "end": v(-2.68, 51.64) * mm});
            skArc(sketch, "E228", {"start": v(-7.5, 51.25) * mm, "mid": v(-6.22, 51.51) * mm, "end": v(-5.08, 52.15) * mm});
            skArc(sketch, "E229", {"start": v(-5.08, 52.15) * mm, "mid": v(-3.93, 51.51) * mm, "end": v(-2.66, 51.18) * mm});
            skArc(sketch, "E230", {"start": v(-5.08, 50.19) * mm, "mid": v(-6.23, 50.75) * mm, "end": v(-7.5, 50.83) * mm});
            skArc(sketch, "E231", {"start": v(-2.71, 50.7) * mm, "mid": v(-3.94, 50.64) * mm, "end": v(-5.08, 50.19) * mm});
            skArc(sketch, "E232", {"start": v(-5.08, 49.56) * mm, "mid": v(-6.22, 50.2) * mm, "end": v(-7.5, 50.45) * mm});
            skArc(sketch, "E233", {"start": v(-2.69, 50.14) * mm, "mid": v(-3.93, 50.05) * mm, "end": v(-5.08, 49.56) * mm});
            skLineSegment(sketch, "E234", {"start": v(-7.5, 51.64) * mm, "end": v(-7.5, 51.25) * mm});
            skLineSegment(sketch, "E235", {"start": v(-7.5, 50.83) * mm, "end": v(-7.5, 50.45) * mm});
            skLineSegment(sketch, "E236", {"start": v(-2.69, 50.14) * mm, "end": v(-2.71, 50.7) * mm});
            skLineSegment(sketch, "E237", {"start": v(-2.66, 51.18) * mm, "end": v(-2.68, 51.64) * mm});
            skArc(sketch, "E238", {"start": v(-7.63, 55.46) * mm, "mid": v(-6.3, 55.92) * mm, "end": v(-5.2, 56.8) * mm});
            skArc(sketch, "E239", {"start": v(-5.2, 56.8) * mm, "mid": v(-4.13, 55.9) * mm, "end": v(-2.8, 55.46) * mm});
            skArc(sketch, "E240", {"start": v(-7.63, 55.06) * mm, "mid": v(-6.34, 55.33) * mm, "end": v(-5.2, 55.97) * mm});
            skArc(sketch, "E241", {"start": v(-5.2, 55.97) * mm, "mid": v(-4.05, 55.33) * mm, "end": v(-2.78, 55) * mm});
            skArc(sketch, "E242", {"start": v(-5.2, 54) * mm, "mid": v(-6.35, 54.56) * mm, "end": v(-7.63, 54.65) * mm});
            skArc(sketch, "E243", {"start": v(-2.83, 54.5) * mm, "mid": v(-4.06, 54.46) * mm, "end": v(-5.2, 54) * mm});
            skArc(sketch, "E244", {"start": v(-5.2, 53.38) * mm, "mid": v(-6.34, 54.02) * mm, "end": v(-7.63, 54.27) * mm});
            skArc(sketch, "E245", {"start": v(-2.8, 53.95) * mm, "mid": v(-4.05, 53.87) * mm, "end": v(-5.2, 53.38) * mm});
            skLineSegment(sketch, "E246", {"start": v(-7.63, 55.46) * mm, "end": v(-7.63, 55.06) * mm});
            skLineSegment(sketch, "E247", {"start": v(-7.63, 54.65) * mm, "end": v(-7.63, 54.27) * mm});
            skLineSegment(sketch, "E248", {"start": v(-2.8, 53.95) * mm, "end": v(-2.83, 54.5) * mm});
            skLineSegment(sketch, "E249", {"start": v(-2.78, 55) * mm, "end": v(-2.8, 55.46) * mm});
            skArc(sketch, "E250", {"start": v(-7.6, 59) * mm, "mid": v(-6.28, 59.47) * mm, "end": v(-5.18, 60.36) * mm});
            skArc(sketch, "E251", {"start": v(-5.18, 60.36) * mm, "mid": v(-4.11, 59.45) * mm, "end": v(-2.78, 59) * mm});
            skArc(sketch, "E252", {"start": v(-7.6, 58.61) * mm, "mid": v(-6.32, 58.88) * mm, "end": v(-5.18, 59.52) * mm});
            skArc(sketch, "E253", {"start": v(-5.18, 59.52) * mm, "mid": v(-4.03, 58.88) * mm, "end": v(-2.76, 58.54) * mm});
            skArc(sketch, "E254", {"start": v(-5.18, 57.55) * mm, "mid": v(-6.33, 58.11) * mm, "end": v(-7.6, 58.2) * mm});
            skArc(sketch, "E255", {"start": v(-2.81, 58.06) * mm, "mid": v(-4.04, 58) * mm, "end": v(-5.18, 57.55) * mm});
            skArc(sketch, "E256", {"start": v(-5.18, 56.93) * mm, "mid": v(-6.32, 57.57) * mm, "end": v(-7.6, 57.82) * mm});
            skArc(sketch, "E257", {"start": v(-2.79, 57.5) * mm, "mid": v(-4.03, 57.42) * mm, "end": v(-5.18, 56.93) * mm});
            skLineSegment(sketch, "E258", {"start": v(-7.6, 59) * mm, "end": v(-7.6, 58.61) * mm});
            skLineSegment(sketch, "E259", {"start": v(-7.6, 58.2) * mm, "end": v(-7.6, 57.82) * mm});
            skLineSegment(sketch, "E260", {"start": v(-2.79, 57.5) * mm, "end": v(-2.81, 58.06) * mm});
            skLineSegment(sketch, "E261", {"start": v(-2.76, 58.54) * mm, "end": v(-2.78, 59) * mm});
            skLineSegment(sketch, "E262", {"start": v(-7.6, 61.22) * mm, "end": v(-7.6, 61.74) * mm});
            skLineSegment(sketch, "E263", {"start": v(-2.88, 61.12) * mm, "end": v(-2.88, 61.6) * mm});
            skArc(sketch, "E264", {"start": v(-5.28, 61.17) * mm, "mid": v(-6.41, 61.57) * mm, "end": v(-7.6, 61.74) * mm});
            skArc(sketch, "E265", {"start": v(-2.88, 61.6) * mm, "mid": v(-4.12, 61.58) * mm, "end": v(-5.28, 61.17) * mm});
            skArc(sketch, "E266", {"start": v(-5.28, 60.72) * mm, "mid": v(-6.4, 61.15) * mm, "end": v(-7.6, 61.22) * mm});
            skArc(sketch, "E267", {"start": v(-2.88, 61.12) * mm, "mid": v(-4.1, 61.02) * mm, "end": v(-5.28, 60.72) * mm});
            skArc(sketch, "E268", {"start": v(-7.6, 62.17) * mm, "mid": v(-6.3, 62.65) * mm, "end": v(-5.28, 63.58) * mm});
            skArc(sketch, "E269", {"start": v(-5.28, 63.58) * mm, "mid": v(-4.21, 62.66) * mm, "end": v(-2.88, 62.22) * mm});
            skArc(sketch, "E270", {"start": v(-7.6, 62.72) * mm, "mid": v(-6.22, 63.32) * mm, "end": v(-5.28, 64.5) * mm});
            skArc(sketch, "E271", {"start": v(-5.28, 64.5) * mm, "mid": v(-4.33, 63.3) * mm, "end": v(-2.88, 62.84) * mm});
            skLineSegment(sketch, "E272", {"start": v(-7.6, 62.17) * mm, "end": v(-7.6, 62.72) * mm});
            skLineSegment(sketch, "E273", {"start": v(-2.88, 62.84) * mm, "end": v(-2.88, 62.22) * mm});
            skSolve(sketch);
        }
        {
            var Q0;
            Q0 = qSketchRegion(id + "F22", true);
            extrude(context, id + "F23", {"entities" : qUnion([Q0]), "endBound" : BoundingType.SYMMETRIC, "depth" : 3.96 * mm, "offsetDistance" : 25.4 * mm});
        }
        {
            var Q0;
            Q0=makeQuery(id+"F23.opExtrude","CAP_EDGE",EDGE,{"disambiguationData":[OSD([sQuery(id+"F22.wireOp",EDGE,"E198")])],"isStart":true});
            var Q1;
            Q1=makeQuery(id+"F23.opExtrude","CAP_EDGE",EDGE,{"disambiguationData":[OSD([sQuery(id+"F22.wireOp",EDGE,"E199")])],"isStart":true});
            var Q2;
            Q2=makeQuery(id+"F23.opExtrude","CAP_EDGE",EDGE,{"disambiguationData":[OSD([sQuery(id+"F22.wireOp",EDGE,"E200")])],"isStart":true});
            var Q3;
            Q3=makeQuery(id+"F23.opExtrude","CAP_EDGE",EDGE,{"disambiguationData":[OSD([sQuery(id+"F22.wireOp",EDGE,"E201")])],"isStart":true});
            var Q4;
            Q4=makeQuery(id+"F23.opExtrude","CAP_EDGE",EDGE,{"disambiguationData":[OSD([sQuery(id+"F22.wireOp",EDGE,"E200")])],"isStart":false});
            var Q5;
            Q5=makeQuery(id+"F23.opExtrude","CAP_EDGE",EDGE,{"disambiguationData":[OSD([sQuery(id+"F22.wireOp",EDGE,"E201")])],"isStart":false});
            var Q6;
            Q6=makeQuery(id+"F23.opExtrude","CAP_EDGE",EDGE,{"disambiguationData":[OSD([sQuery(id+"F22.wireOp",EDGE,"E198")])],"isStart":false});
            var Q7;
            Q7=makeQuery(id+"F23.opExtrude","CAP_EDGE",EDGE,{"disambiguationData":[OSD([sQuery(id+"F22.wireOp",EDGE,"E199")])],"isStart":false});
            var Q8;
            Q8=makeQuery(id+"F23.opExtrude","CAP_EDGE",EDGE,{"disambiguationData":[OSD([sQuery(id+"F22.wireOp",EDGE,"E212")])],"isStart":false});
            var Q9;
            Q9=makeQuery(id+"F23.opExtrude","CAP_EDGE",EDGE,{"disambiguationData":[OSD([sQuery(id+"F22.wireOp",EDGE,"E211")])],"isStart":false});
            var Q10;
            Q10=makeQuery(id+"F23.opExtrude","CAP_EDGE",EDGE,{"disambiguationData":[OSD([sQuery(id+"F22.wireOp",EDGE,"E213")])],"isStart":false});
            var Q11;
            Q11=makeQuery(id+"F23.opExtrude","CAP_EDGE",EDGE,{"disambiguationData":[OSD([sQuery(id+"F22.wireOp",EDGE,"E210")])],"isStart":false});
            var Q12;
            Q12=makeQuery(id+"F23.opExtrude","CAP_EDGE",EDGE,{"disambiguationData":[OSD([sQuery(id+"F22.wireOp",EDGE,"E211")])],"isStart":true});
            var Q13;
            Q13=makeQuery(id+"F23.opExtrude","CAP_EDGE",EDGE,{"disambiguationData":[OSD([sQuery(id+"F22.wireOp",EDGE,"E212")])],"isStart":true});
            var Q14;
            Q14=makeQuery(id+"F23.opExtrude","CAP_EDGE",EDGE,{"disambiguationData":[OSD([sQuery(id+"F22.wireOp",EDGE,"E213")])],"isStart":true});
            var Q15;
            Q15=makeQuery(id+"F23.opExtrude","CAP_EDGE",EDGE,{"disambiguationData":[OSD([sQuery(id+"F22.wireOp",EDGE,"E210")])],"isStart":true});
            var Q16;
            Q16=makeQuery(id+"F23.opExtrude","CAP_EDGE",EDGE,{"disambiguationData":[OSD([sQuery(id+"F22.wireOp",EDGE,"E224")])],"isStart":false});
            var Q17;
            Q17=makeQuery(id+"F23.opExtrude","CAP_EDGE",EDGE,{"disambiguationData":[OSD([sQuery(id+"F22.wireOp",EDGE,"E224")])],"isStart":true});
            var Q18;
            Q18=makeQuery(id+"F23.opExtrude","CAP_EDGE",EDGE,{"disambiguationData":[OSD([sQuery(id+"F22.wireOp",EDGE,"E223")])],"isStart":false});
            var Q19;
            Q19=makeQuery(id+"F23.opExtrude","CAP_EDGE",EDGE,{"disambiguationData":[OSD([sQuery(id+"F22.wireOp",EDGE,"E223")])],"isStart":true});
            var Q20;
            Q20=makeQuery(id+"F23.opExtrude","CAP_EDGE",EDGE,{"disambiguationData":[OSD([sQuery(id+"F22.wireOp",EDGE,"E225")])],"isStart":true});
            var Q21;
            Q21=makeQuery(id+"F23.opExtrude","CAP_EDGE",EDGE,{"disambiguationData":[OSD([sQuery(id+"F22.wireOp",EDGE,"E225")])],"isStart":false});
            var Q22;
            Q22=makeQuery(id+"F23.opExtrude","CAP_EDGE",EDGE,{"disambiguationData":[OSD([sQuery(id+"F22.wireOp",EDGE,"E222")])],"isStart":true});
            var Q23;
            Q23=makeQuery(id+"F23.opExtrude","CAP_EDGE",EDGE,{"disambiguationData":[OSD([sQuery(id+"F22.wireOp",EDGE,"E222")])],"isStart":false});
            var Q24;
            Q24=makeQuery(id+"F23.opExtrude","CAP_EDGE",EDGE,{"disambiguationData":[OSD([sQuery(id+"F22.wireOp",EDGE,"E235")])],"isStart":true});
            var Q25;
            Q25=makeQuery(id+"F23.opExtrude","CAP_EDGE",EDGE,{"disambiguationData":[OSD([sQuery(id+"F22.wireOp",EDGE,"E236")])],"isStart":true});
            var Q26;
            Q26=makeQuery(id+"F23.opExtrude","CAP_EDGE",EDGE,{"disambiguationData":[OSD([sQuery(id+"F22.wireOp",EDGE,"E234")])],"isStart":true});
            var Q27;
            Q27=makeQuery(id+"F23.opExtrude","CAP_EDGE",EDGE,{"disambiguationData":[OSD([sQuery(id+"F22.wireOp",EDGE,"E237")])],"isStart":true});
            var Q28;
            Q28=makeQuery(id+"F23.opExtrude","CAP_EDGE",EDGE,{"disambiguationData":[OSD([sQuery(id+"F22.wireOp",EDGE,"E235")])],"isStart":false});
            var Q29;
            Q29=makeQuery(id+"F23.opExtrude","CAP_EDGE",EDGE,{"disambiguationData":[OSD([sQuery(id+"F22.wireOp",EDGE,"E234")])],"isStart":false});
            var Q30;
            Q30=makeQuery(id+"F23.opExtrude","CAP_EDGE",EDGE,{"disambiguationData":[OSD([sQuery(id+"F22.wireOp",EDGE,"E236")])],"isStart":false});
            var Q31;
            Q31=makeQuery(id+"F23.opExtrude","CAP_EDGE",EDGE,{"disambiguationData":[OSD([sQuery(id+"F22.wireOp",EDGE,"E237")])],"isStart":false});
            var Q32;
            Q32=makeQuery(id+"F23.opExtrude","CAP_EDGE",EDGE,{"disambiguationData":[OSD([sQuery(id+"F22.wireOp",EDGE,"E247")])],"isStart":false});
            var Q33;
            Q33=makeQuery(id+"F23.opExtrude","CAP_EDGE",EDGE,{"disambiguationData":[OSD([sQuery(id+"F22.wireOp",EDGE,"E248")])],"isStart":false});
            var Q34;
            Q34=makeQuery(id+"F23.opExtrude","CAP_EDGE",EDGE,{"disambiguationData":[OSD([sQuery(id+"F22.wireOp",EDGE,"E248")])],"isStart":true});
            var Q35;
            Q35=makeQuery(id+"F23.opExtrude","CAP_EDGE",EDGE,{"disambiguationData":[OSD([sQuery(id+"F22.wireOp",EDGE,"E247")])],"isStart":true});
            var Q36;
            Q36=makeQuery(id+"F23.opExtrude","CAP_EDGE",EDGE,{"disambiguationData":[OSD([sQuery(id+"F22.wireOp",EDGE,"E246")])],"isStart":true});
            var Q37;
            Q37=makeQuery(id+"F23.opExtrude","CAP_EDGE",EDGE,{"disambiguationData":[OSD([sQuery(id+"F22.wireOp",EDGE,"E246")])],"isStart":false});
            var Q38;
            Q38=makeQuery(id+"F23.opExtrude","CAP_EDGE",EDGE,{"disambiguationData":[OSD([sQuery(id+"F22.wireOp",EDGE,"E249")])],"isStart":true});
            var Q39;
            Q39=makeQuery(id+"F23.opExtrude","CAP_EDGE",EDGE,{"disambiguationData":[OSD([sQuery(id+"F22.wireOp",EDGE,"E249")])],"isStart":false});
            var Q40;
            Q40=makeQuery(id+"F23.opExtrude","CAP_EDGE",EDGE,{"disambiguationData":[OSD([sQuery(id+"F22.wireOp",EDGE,"E260")])],"isStart":false});
            var Q41;
            Q41=makeQuery(id+"F23.opExtrude","CAP_EDGE",EDGE,{"disambiguationData":[OSD([sQuery(id+"F22.wireOp",EDGE,"E260")])],"isStart":true});
            var Q42;
            Q42=makeQuery(id+"F23.opExtrude","CAP_EDGE",EDGE,{"disambiguationData":[OSD([sQuery(id+"F22.wireOp",EDGE,"E259")])],"isStart":true});
            var Q43;
            Q43=makeQuery(id+"F23.opExtrude","CAP_EDGE",EDGE,{"disambiguationData":[OSD([sQuery(id+"F22.wireOp",EDGE,"E259")])],"isStart":false});
            var Q44;
            Q44=makeQuery(id+"F23.opExtrude","CAP_EDGE",EDGE,{"disambiguationData":[OSD([sQuery(id+"F22.wireOp",EDGE,"E258")])],"isStart":false});
            var Q45;
            Q45=makeQuery(id+"F23.opExtrude","CAP_EDGE",EDGE,{"disambiguationData":[OSD([sQuery(id+"F22.wireOp",EDGE,"E258")])],"isStart":true});
            var Q46;
            Q46=makeQuery(id+"F23.opExtrude","CAP_EDGE",EDGE,{"disambiguationData":[OSD([sQuery(id+"F22.wireOp",EDGE,"E261")])],"isStart":false});
            var Q47;
            Q47=makeQuery(id+"F23.opExtrude","CAP_EDGE",EDGE,{"disambiguationData":[OSD([sQuery(id+"F22.wireOp",EDGE,"E261")])],"isStart":true});
            var Q48;
            Q48=makeQuery(id+"F23.opExtrude","CAP_EDGE",EDGE,{"disambiguationData":[OSD([sQuery(id+"F22.wireOp",EDGE,"E263")])],"isStart":false});
            var Q49;
            Q49=makeQuery(id+"F23.opExtrude","CAP_EDGE",EDGE,{"disambiguationData":[OSD([sQuery(id+"F22.wireOp",EDGE,"E263")])],"isStart":true});
            var Q50;
            Q50=makeQuery(id+"F23.opExtrude","CAP_EDGE",EDGE,{"disambiguationData":[OSD([sQuery(id+"F22.wireOp",EDGE,"E262")])],"isStart":false});
            var Q51;
            Q51=makeQuery(id+"F23.opExtrude","CAP_EDGE",EDGE,{"disambiguationData":[OSD([sQuery(id+"F22.wireOp",EDGE,"E262")])],"isStart":true});
            var Q52;
            Q52=makeQuery(id+"F23.opExtrude","CAP_EDGE",EDGE,{"disambiguationData":[OSD([sQuery(id+"F22.wireOp",EDGE,"E272")])],"isStart":true});
            var Q53;
            Q53=makeQuery(id+"F23.opExtrude","CAP_EDGE",EDGE,{"disambiguationData":[OSD([sQuery(id+"F22.wireOp",EDGE,"E272")])],"isStart":false});
            var Q54;
            Q54=makeQuery(id+"F23.opExtrude","CAP_EDGE",EDGE,{"disambiguationData":[OSD([sQuery(id+"F22.wireOp",EDGE,"E273")])],"isStart":true});
            var Q55;
            Q55=makeQuery(id+"F23.opExtrude","CAP_EDGE",EDGE,{"disambiguationData":[OSD([sQuery(id+"F22.wireOp",EDGE,"E273")])],"isStart":false});
            fillet(context, id + "F24", {"entities" : qUnion([Q0, Q1, Q2, Q3, Q4, Q5, Q6, Q7, Q8, Q9, Q10, Q11, Q12, Q13, Q14, Q15, Q16, Q17, Q18, Q19, Q20, Q21, Q22, Q23, Q24, Q25, Q26, Q27, Q28, Q29, Q30, Q31, Q32, Q33, Q34, Q35, Q36, Q37, Q38, Q39, Q40, Q41, Q42, Q43, Q44, Q45, Q46, Q47, Q48, Q49, Q50, Q51, Q52, Q53, Q54, Q55]), "radius" : 3.07 * mm, "tangentPropagation" : true, "allowEdgeOverflow" : false});
        }
        {
            var Q0;
            Q0=makeQuery(id+"F14.opExtrude","CAP_FACE",FACE,{"disambiguationData":[OSD([sQuery(id+"F0.wireOp",EDGE,"E66"),sQuery(id+"F0.wireOp",EDGE,"E67"),sQuery(id+"F0.wireOp",EDGE,"E76"),sQuery(id+"F0.wireOp",EDGE,"E79"),sQuery(id+"F0.wireOp",EDGE,"E80"),sQuery(id+"F0.wireOp",EDGE,"E81"),sQuery(id+"F0.wireOp",EDGE,"E82"),sQuery(id+"F0.wireOp",EDGE,"E83"),sQuery(id+"F0.wireOp",EDGE,"E90"),sQuery(id+"F0.wireOp",EDGE,"E91"),sQuery(id+"F0.wireOp",EDGE,"E92"),sQuery(id+"F0.wireOp",EDGE,"E93"),sQuery(id+"F0.wireOp",EDGE,"E94"),sQuery(id+"F0.wireOp",EDGE,"E95.MirrorCS"),sQuery(id+"F0.wireOp",EDGE,"E96.MirrorCS"),sQuery(id+"F0.wireOp",EDGE,"E97.MirrorCS"),sQuery(id+"F0.wireOp",EDGE,"E98.MirrorCS"),sQuery(id+"F0.wireOp",EDGE,"E99.MirrorCS"),sQuery(id+"F0.wireOp",EDGE,"E100"),sQuery(id+"F0.wireOp",EDGE,"E101"),sQuery(id+"F0.wireOp",EDGE,"E102"),sQuery(id+"F0.wireOp",EDGE,"E103"),sQuery(id+"F0.wireOp",EDGE,"E104")])],"isStart":false});
            var sketch = newSketch(context, id + "F25", { "sketchPlane" : qUnion([Q0])});
            skLineSegment(sketch, "E274", {"start": v(-8.92, 3.9) * mm, "end": v(-7.08, 0.66) * mm});
            skLineSegment(sketch, "E275", {"start": v(-7.08, 0.66) * mm, "end": v(-5.26, 3.86) * mm});
            skLineSegment(sketch, "E276", {"start": v(-5.26, 3.86) * mm, "end": v(-8.92, 3.9) * mm});
            skLineSegment(sketch, "E277", {"start": v(-5.14, 3.86) * mm, "end": v(-3.3, 0.61) * mm});
            skLineSegment(sketch, "E278", {"start": v(-3.3, 0.61) * mm, "end": v(-1.4, 3.9) * mm});
            skLineSegment(sketch, "E279", {"start": v(-1.4, 3.9) * mm, "end": v(-5.14, 3.86) * mm});
            skLineSegment(sketch, "E280", {"start": v(-7.08, 0.58) * mm, "end": v(-3.35, 0.58) * mm});
            skLineSegment(sketch, "E281", {"start": v(-3.35, 0.58) * mm, "end": v(-5.13, -2.57) * mm});
            skLineSegment(sketch, "E282", {"start": v(-5.13, -2.57) * mm, "end": v(-7.08, 0.58) * mm});
            skSolve(sketch);
        }
        {
            var Q0;
            Q0=makeQuery(id+"F25.imprint","IMPRINT",FACE,{"disambiguationData":[TD([[makeQuery(id+"F25.imprint","IMPRINT",EDGE,{"derivedFrom":sQuery(id+"F25.wireOp",EDGE,"E274")}),1.0]])]});
            var Q1;
            Q1=makeQuery(id+"F25.imprint","IMPRINT",FACE,{"disambiguationData":[TD([[makeQuery(id+"F25.imprint","IMPRINT",EDGE,{"derivedFrom":sQuery(id+"F25.wireOp",EDGE,"E277")}),1.0]])]});
            var Q2;
            Q2=makeQuery(id+"F25.imprint","IMPRINT",FACE,{"disambiguationData":[TD([[makeQuery(id+"F25.imprint","IMPRINT",EDGE,{"derivedFrom":sQuery(id+"F25.wireOp",EDGE,"E280")}),-1.0]])]});
            extrude(context, id + "F26", {"entities" : qUnion([Q0, Q1, Q2]), "operationType" : NewBodyOperationType.ADD, "depth" : 0.33 * mm, "offsetDistance" : 25.4 * mm, "hasSecondDirection" : true, "secondDirectionOppositeDirection" : true, "secondDirectionDepth" : 3 * mm});
        }
    });
